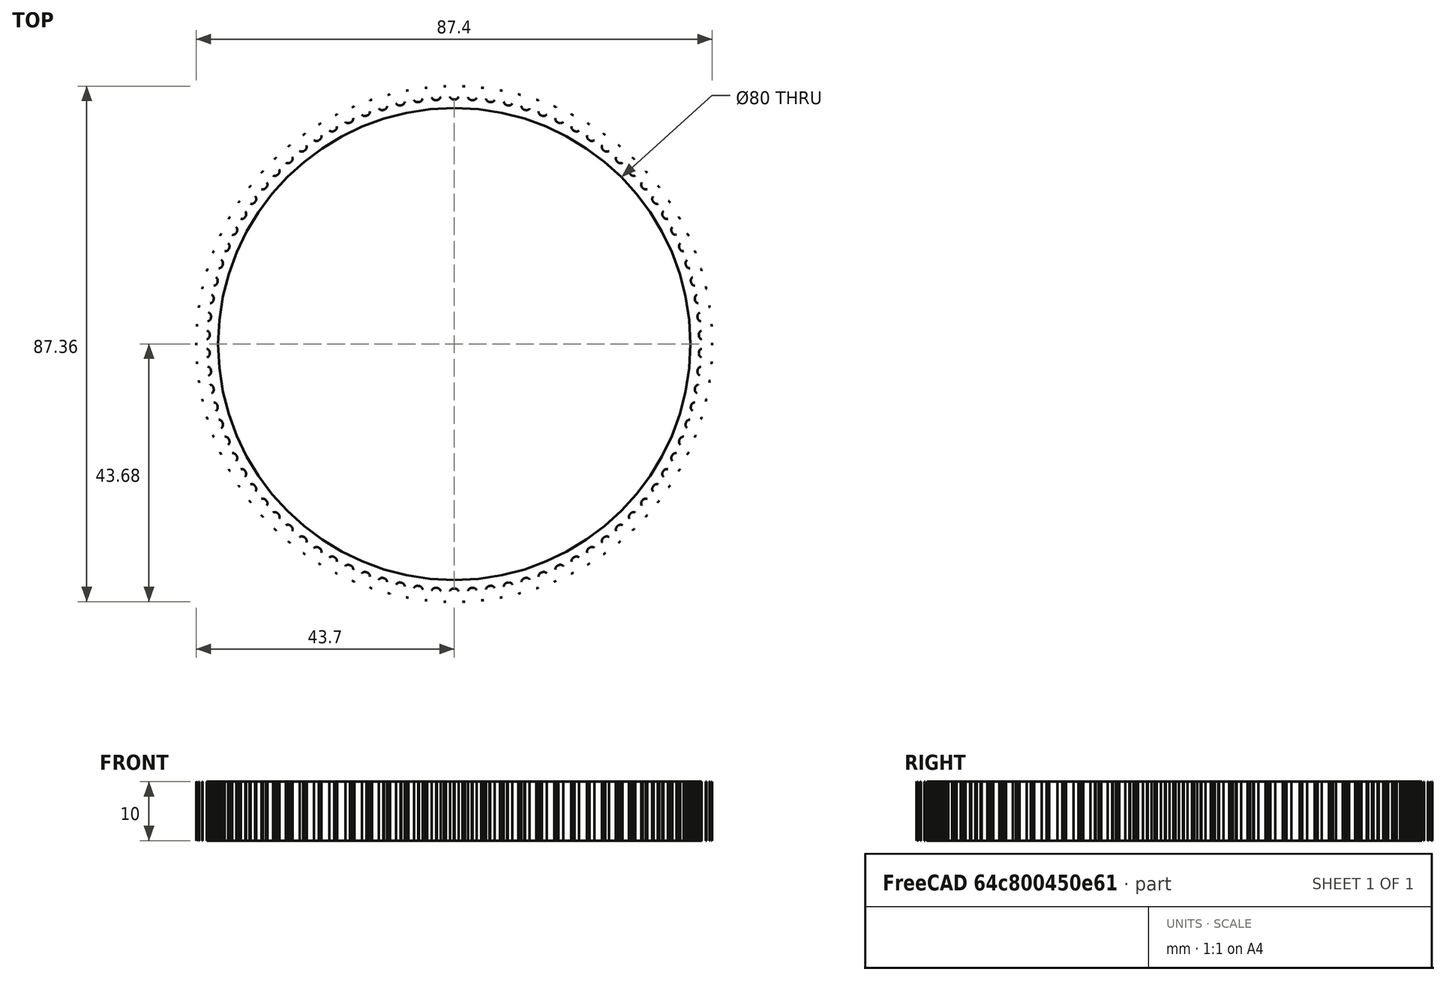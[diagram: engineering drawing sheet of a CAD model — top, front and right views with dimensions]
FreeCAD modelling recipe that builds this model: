
FCSTD DOCUMENT  (FreeCAD 0.19R24276 (Git))
Label: In_gear_t86_d80_V4
License: All rights reserved
LicenseURL: http://en.wikipedia.org/wiki/All_rights_reserved
objects: Part::Extrusion×2, Part::Part2DObjectPython×1, Part::Offset2D×1, Part::Cylinder×1, Part::Cut×1
note: 6 computed .brp shape members not serialized (recipe doc carries the construction recipe); baked Part::Feature solids carry a one-line shape summary decoded from their .brp

FEATURE [Part::Part2DObjectPython] InvoluteGear  # Draft 2D object (typed FeaturePython)
  ExternalGear = true
  HighPrecision = true
  Modules = 1
  NumberOfTeeth = 86
  PressureAngle = 20
FEATURE [Part::Offset2D] Offset2D
  Fill = false
  Intersection = false
  Join = 0
  Mode = 1
  SelfIntersection = false
  Source = -> InvoluteGear
  Value = -0.3
FEATURE [Part::Cylinder] Cylinder  label="Цилиндр"
  Angle = 360
  AttacherType = Attacher::AttachEngine3D
  Height = 10
  Radius = 40
FEATURE [Part::Extrusion] Extrude
  Base = -> Offset2D
  Dir = (0,0,1)
  DirMode = 2
  FaceMakerClass = Part::FaceMakerBullseye
  LengthFwd = 10
  LengthRev = 0
  Solid = true
  Symmetric = false
FEATURE [Part::Extrusion] Extrude001
  Base = -> Offset2D
  Dir = (0,0,1)
  DirMode = 2
  FaceMakerClass = Part::FaceMakerBullseye
  LengthFwd = 10
  LengthRev = 0
  Solid = true
  Symmetric = false
FEATURE [Part::Cut] Cut
  Base = -> Extrude
  Tool = -> Cylinder
